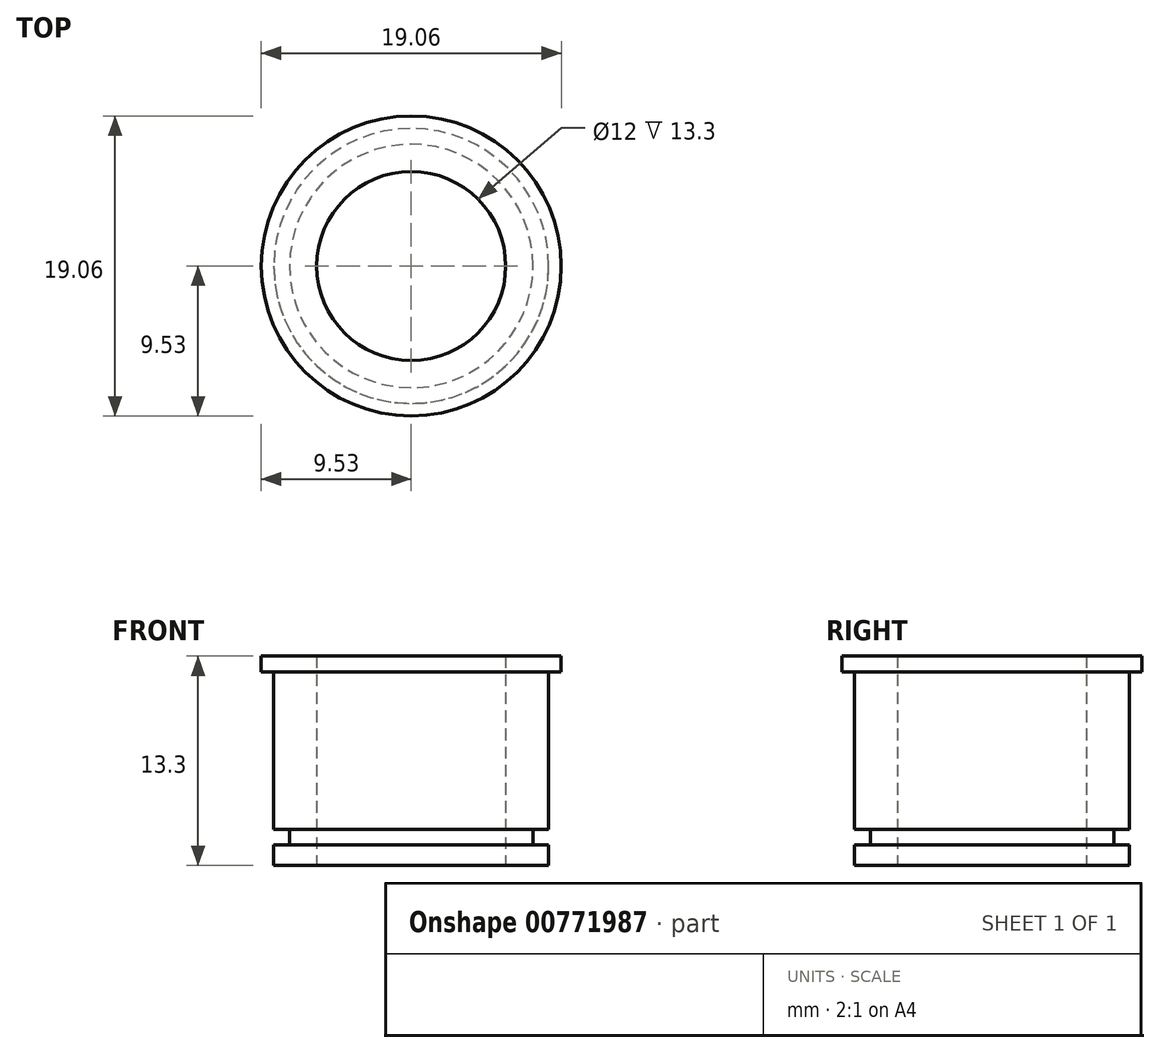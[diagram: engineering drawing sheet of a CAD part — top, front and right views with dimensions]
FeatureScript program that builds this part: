
annotation { "Feature Type Name" : "Feature", "Feature Type Description" : "" }
export const myFeature = defineFeature(function(context is Context, id is Id, definition is map)
    precondition{}
    {
        {
            var Q0;
            Q0=qCreatedBy(makeId("Top.planeOp"),FACE);
            var sketch = newSketch(context, id + "F0", { "sketchPlane" : qUnion([Q0])});
            skCircle(sketch, "E0", {"center": v(0, 0) * mm, "radius": 8.73 * mm});
            skCircle(sketch, "E1", {"center": v(0, 0) * mm, "radius": 6 * mm});
            skSolve(sketch);
        }
        {
            var Q0;
            Q0 = qSketchRegion(id + "F0", true);
            extrude(context, id + "F1", {"entities" : qUnion([Q0]), "depth" : 12.3 * mm, "offsetDistance" : 25 * mm});
        }
        {
            var Q0;
            Q0=makeQuery(id+"F1.opExtrude","CAP_FACE",FACE,{"disambiguationData":[OSD([sQuery(id+"F0.wireOp",EDGE,"E0"),sQuery(id+"F0.wireOp",EDGE,"E1")])],"isStart":false});
            var sketch = newSketch(context, id + "F2", { "sketchPlane" : qUnion([Q0])});
            skCircle(sketch, "E2", {"center": v(0, 0) * mm, "radius": 9.53 * mm});
            skCircle(sketch, "E3.0", {"center": v(0, 0) * mm, "radius": 6 * mm});
            skSolve(sketch);
        }
        {
            var Q0;
            Q0 = qSketchRegion(id + "F2", true);
            extrude(context, id + "F3", {"entities" : qUnion([Q0]), "operationType" : NewBodyOperationType.ADD, "depth" : 1 * mm, "offsetDistance" : 25.4 * mm});
        }
        {
            var Q0;
            Q0=qCreatedBy(makeId("Front.planeOp"),FACE);
            var sketch = newSketch(context, id + "F4", { "sketchPlane" : qUnion([Q0])});
            skLineSegment(sketch, "E4", {"start": v(0, 26.48) * mm, "end": v(0, -12.19) * mm, "construction": true});
            skLineSegment(sketch, "E5.bottom", {"start": v(-7.73, 1.3) * mm, "end": v(-9.73, 1.3) * mm});
            skLineSegment(sketch, "E5.top", {"start": v(-7.73, 2.3) * mm, "end": v(-9.73, 2.3) * mm});
            skLineSegment(sketch, "E5.left", {"start": v(-7.73, 1.3) * mm, "end": v(-7.73, 2.3) * mm});
            skLineSegment(sketch, "E5.right", {"start": v(-9.73, 1.3) * mm, "end": v(-9.73, 2.3) * mm});
            skPoint(sketch, "E5.middle", {"position": v(-8.73, 1.8) * mm});
            skSolve(sketch);
        }
        {
            var Q0;
            Q0 = qSketchRegion(id + "F4", true);
            var Q1;
            Q1=sQuery(id+"F4.wireOp",EDGE,"E4");
            revolve(context, id + "F5", {"operationType" : NewBodyOperationType.REMOVE, "surfaceOperationType" : NewSurfaceOperationType.NEW, "entities" : qUnion([Q0]), "axis" : qUnion([Q1]), "revolveType" : RevolveType.FULL, "oppositeDirection" : true});
        }
    });
